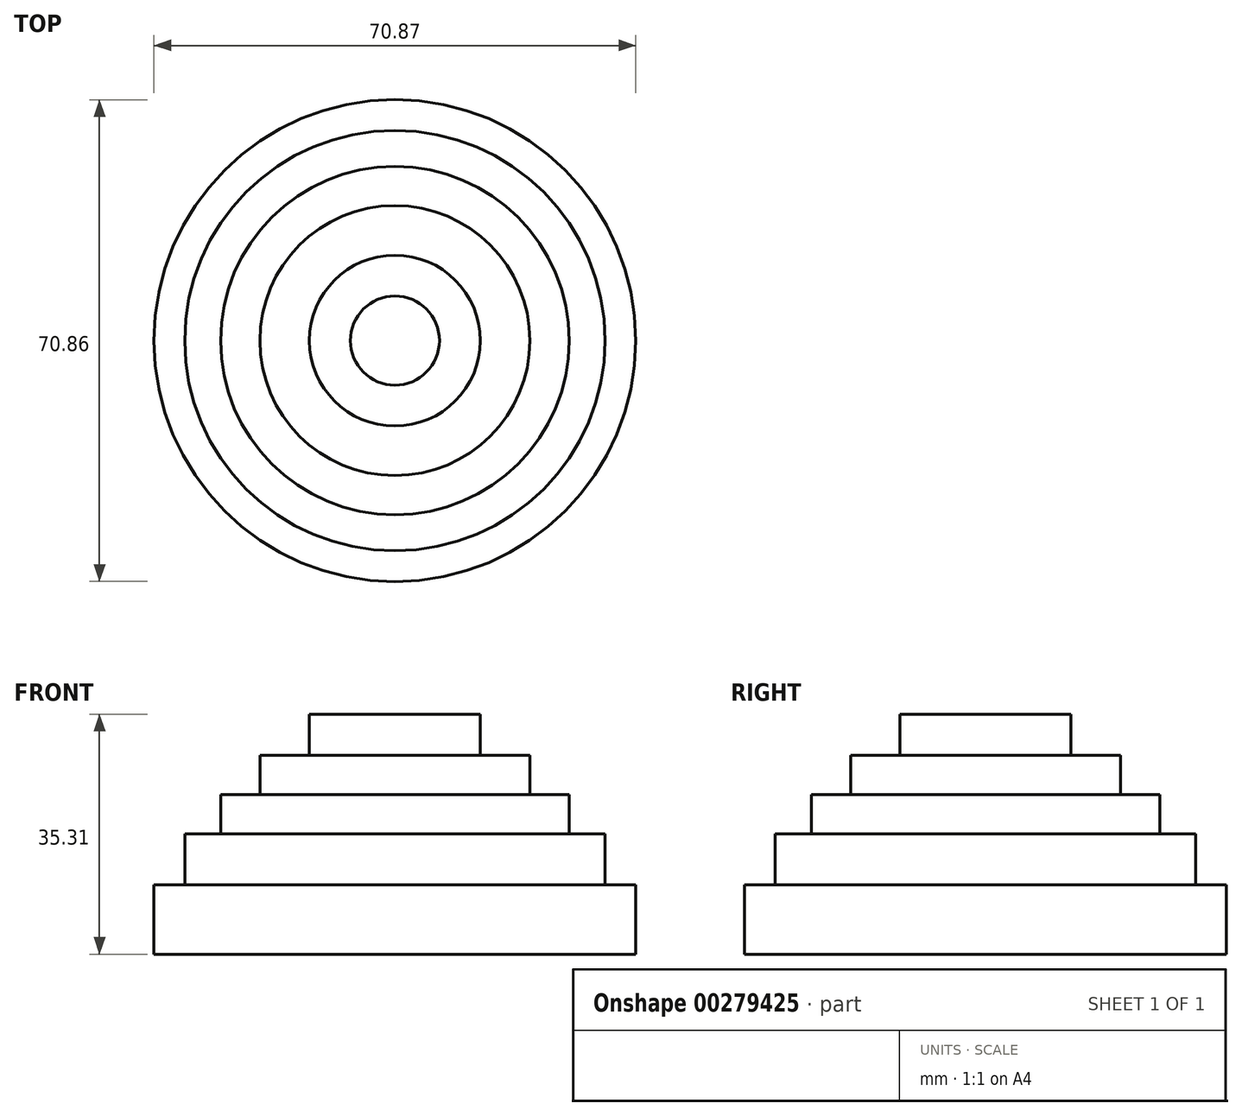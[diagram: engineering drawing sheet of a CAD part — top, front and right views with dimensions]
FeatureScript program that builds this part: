
annotation { "Feature Type Name" : "Feature", "Feature Type Description" : "" }
export const myFeature = defineFeature(function(context is Context, id is Id, definition is map)
    precondition{}
    {
        {
            var Q0;
            Q0=qCreatedBy(makeId("Front.planeOp"),FACE);
            var sketch = newSketch(context, id + "F0", { "sketchPlane" : qUnion([Q0])});
            skLineSegment(sketch, "E0", {"start": v(-28.88, 0) * mm, "end": v(-28.88, 10.18) * mm});
            skLineSegment(sketch, "E1", {"start": v(-28.88, 10.18) * mm, "end": v(-24.35, 10.18) * mm});
            skLineSegment(sketch, "E2", {"start": v(-24.35, 10.18) * mm, "end": v(-24.35, 17.72) * mm});
            skLineSegment(sketch, "E3", {"start": v(-24.35, 17.72) * mm, "end": v(-19.08, 17.72) * mm});
            skLineSegment(sketch, "E4", {"start": v(-19.08, 17.72) * mm, "end": v(-19.08, 23.5) * mm});
            skLineSegment(sketch, "E5", {"start": v(-19.08, 23.5) * mm, "end": v(-13.3, 23.5) * mm});
            skLineSegment(sketch, "E6", {"start": v(-13.3, 23.5) * mm, "end": v(-13.3, 29.28) * mm});
            skLineSegment(sketch, "E7", {"start": v(-13.3, 29.28) * mm, "end": v(-6, 29.28) * mm});
            skLineSegment(sketch, "E8", {"start": v(-6, 29.28) * mm, "end": v(-6, 35.3) * mm});
            skLineSegment(sketch, "E9", {"start": v(-6, 35.3) * mm, "end": v(0, 35.3) * mm});
            skLineSegment(sketch, "E10", {"start": v(6.56, 35.56) * mm, "end": v(6.56, 0) * mm});
            skSolve(sketch);
        }
        {
            var Q0;
            Q0 = qSketchRegion(id + "F0", true);
            var Q1;
            Q1=sQuery(id+"F0.wireOp",EDGE,"E0");
            var Q2;
            Q2=sQuery(id+"F0.wireOp",EDGE,"E2");
            var Q3;
            Q3=sQuery(id+"F0.wireOp",EDGE,"E1");
            var Q4;
            Q4=sQuery(id+"F0.wireOp",EDGE,"E3");
            var Q5;
            Q5=sQuery(id+"F0.wireOp",EDGE,"E4");
            var Q6;
            Q6=sQuery(id+"F0.wireOp",EDGE,"E5");
            var Q7;
            Q7=sQuery(id+"F0.wireOp",EDGE,"E6");
            var Q8;
            Q8=sQuery(id+"F0.wireOp",EDGE,"E7");
            var Q9;
            Q9=sQuery(id+"F0.wireOp",EDGE,"E8");
            var Q10;
            Q10=sQuery(id+"F0.wireOp",EDGE,"E9");
            var Q11;
            Q11=sQuery(id+"F0.wireOp",EDGE,"E10");
            revolve(context, id + "F1", {"bodyType" : ToolBodyType.SURFACE, "entities" : qUnion([Q0]), "surfaceEntities" : qUnion([Q1, Q2, Q3, Q4, Q5, Q6, Q7, Q8, Q9, Q10]), "axis" : qUnion([Q11]), "revolveType" : RevolveType.FULL});
        }
    });
